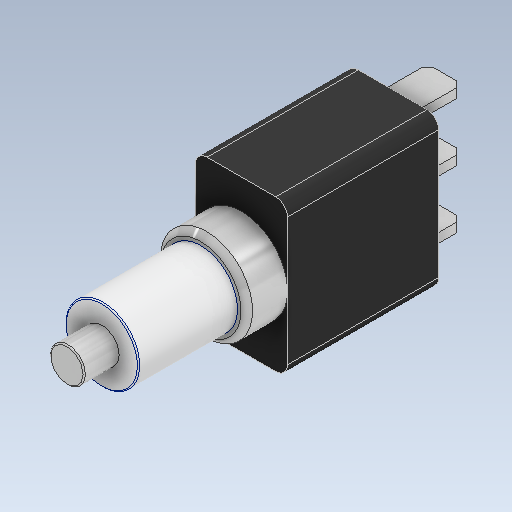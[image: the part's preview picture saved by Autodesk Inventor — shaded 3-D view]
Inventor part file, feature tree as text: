
AUTODESK INVENTOR PART (.ipt)
format: ipt  version: 2021 (Build 250183000, 183)  size: 225,792 bytes
history: native  units: mm
features: extrude x5, sketch x5, fillet x3, chamfer x2
ambient origin geometry x8: Origin, YZ Plane, XZ Plane, XY Plane, X Axis, Y Axis, Z Axis, Center Point
bodies: Solid1 (feature_tree), Solid2 (feature_tree), Solid3 (feature_tree), Solid4 (feature_tree), Solid5 (feature_tree)
feature tree (15):
  extrude  "Extrusion1"  Depth=7.9mm
  extrude  "Extrusion2"  Depth=1.5mm
  extrude  "Extrusion3"  Depth=0.8mm
  extrude  "Extrusion4"  Depth=0.8mm
  extrude  "Extrusion5"  Depth=4.5mm TaperAngle=0.0deg
  chamfer  "Chamfer1"  Distance=3.5mm
  fillet  "Fillet1"  Radius=6.3mm
  chamfer  "Chamfer2"  Distance=8.5mm
  fillet  "Fillet2"  Radius=3.0mm
  fillet  "Fillet3"  Radius=3.0mm
  sketch  "Sketch1"  dims[d0=13.0mm d1=7.9mm]
  sketch  "Sketch2"  dims[d2=13.0mm d3=0.0mm d4=1.5mm]
  sketch  "Sketch3"  dims[d5=1.5mm d6=0.8mm]
  sketch  "Sketch4"  dims[d7=0.8mm d8=0.8mm]
  sketch  "Sketch5"  dims[d9=3.0mm d10=4.5mm d11=0.0mm d13=3.5mm d14=0.0mm d15=6.3mm d16=8.5mm d17=0.0mm d18=3.0mm d19=3.0mm d20=0.0mm d21=0.5mm d22=2.0mm d23=45.0deg d24=1.0mm d25=0.5mm d26=2.0mm d27=45.0deg d28=0.1mm d29=0.1mm]
